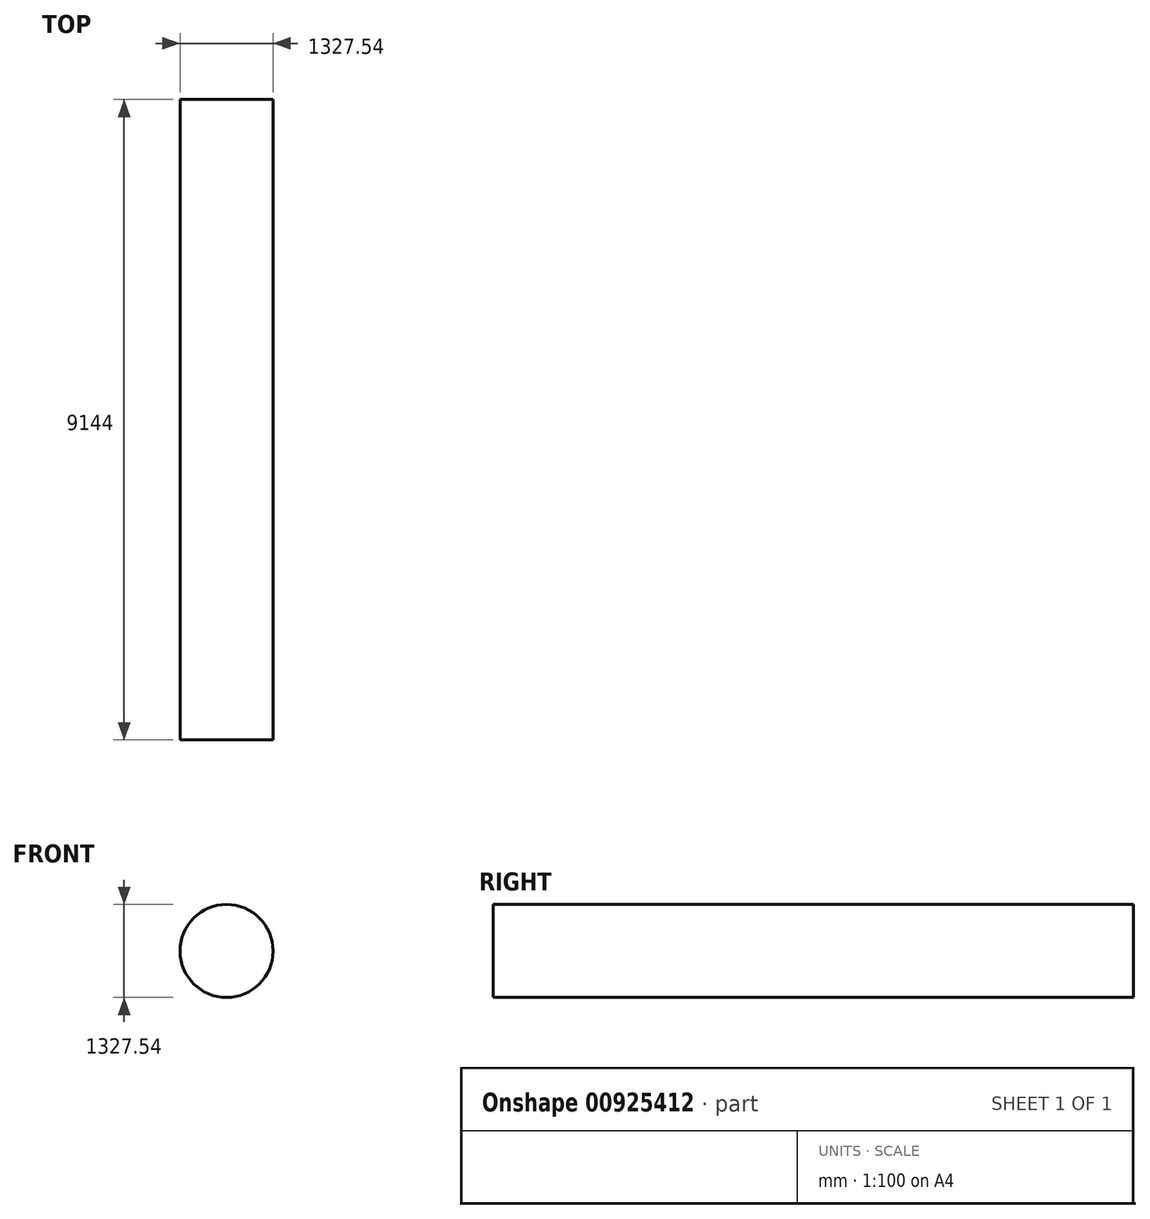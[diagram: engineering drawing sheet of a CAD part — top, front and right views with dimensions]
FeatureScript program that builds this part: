
annotation { "Feature Type Name" : "Feature", "Feature Type Description" : "" }
export const myFeature = defineFeature(function(context is Context, id is Id, definition is map)
    precondition{}
    {
        {
            var Q0;
            Q0=qCreatedBy(makeId("Front.planeOp"),FACE);
            var sketch = newSketch(context, id + "F0", { "sketchPlane" : qUnion([Q0])});
            skCircle(sketch, "E0", {"center": v(0, 0) * mm, "radius": 663.77 * mm});
            skSolve(sketch);
        }
        {
            var Q0;
            Q0=sQuery(id+"F0.wireOp",EDGE,"E0");
            extrude(context, id + "F1", {"bodyType" : ToolBodyType.SURFACE, "surfaceEntities" : qUnion([Q0]), "depth" : 9144 * mm, "offsetDistance" : 25.4 * mm});
        }
    });
